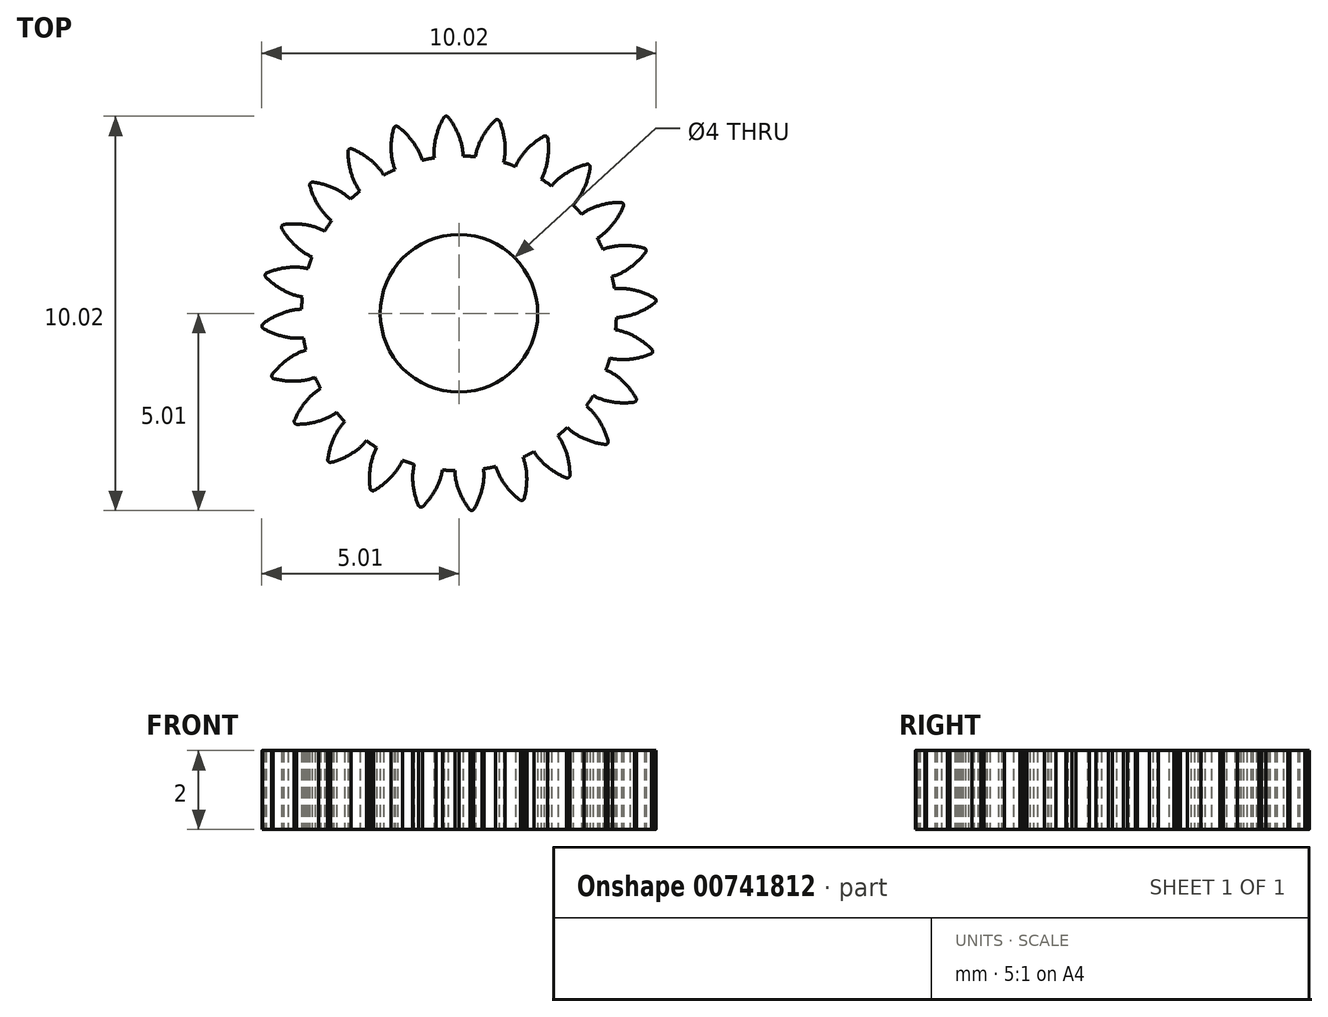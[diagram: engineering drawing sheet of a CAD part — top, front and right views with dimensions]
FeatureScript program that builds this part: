
annotation { "Feature Type Name" : "Feature", "Feature Type Description" : "" }
export const myFeature = defineFeature(function(context is Context, id is Id, definition is map)
    precondition{}
    {
        {
            var Q0;
            Q0=qCreatedBy(makeId("Top.planeOp"),FACE);
            var sketch = newSketch(context, id + "F0", { "sketchPlane" : qUnion([Q0])});
            skCircle(sketch, "E0", {"center": v(0, 0) * mm, "radius": 4 * mm});
            skCircle(sketch, "E1", {"center": v(0, 0) * mm, "radius": 4.5 * mm, "construction": true});
            skCircle(sketch, "E2", {"center": v(0, 0) * mm, "radius": 5 * mm, "construction": true});
            skLineSegment(sketch, "E3", {"start": v(0, 0) * mm, "end": v(0, 7.18) * mm, "construction": true});
            skLineSegment(sketch, "E4", {"start": v(0, 0) * mm, "end": v(-0.5, 7.73) * mm, "construction": true});
            skLineSegment(sketch, "E5", {"start": v(0, 4.5) * mm, "end": v(-8.8, 4.5) * mm, "construction": true});
            skLineSegment(sketch, "E6", {"start": v(0, 4.5) * mm, "end": v(-8.5, 1.41) * mm, "construction": true});
            skCircle(sketch, "E7", {"center": v(0, 0) * mm, "radius": 4.23 * mm, "construction": true});
            skCircle(sketch, "E8", {"center": v(0, 4.5) * mm, "radius": 1.75 * mm, "construction": true});
            skCircle(sketch, "E9", {"center": v(-1.64, 3.9) * mm, "radius": 1.75 * mm, "construction": true});
            skArc(sketch, "E10", {"start": v(0.1, 4) * mm, "mid": v(0.07, 4.25) * mm, "end": v(0, 4.5) * mm});
            skArc(sketch, "E11", {"start": v(0, 4.5) * mm, "mid": v(-0.12, 4.76) * mm, "end": v(-0.28, 5) * mm});
            skArc(sketch, "E12.MirrorCS", {"start": v(-0.59, 4.46) * mm, "mid": v(-0.5, 4.73) * mm, "end": v(-0.38, 4.99) * mm});
            skArc(sketch, "E13.MirrorCS", {"start": v(-0.63, 3.95) * mm, "mid": v(-0.63, 4.2) * mm, "end": v(-0.59, 4.46) * mm});
            skArc(sketch, "E14", {"start": v(-0.28, 5) * mm, "mid": v(-0.33, 5) * mm, "end": v(-0.38, 4.99) * mm});
            skCircle(sketch, "E15", {"center": v(0, 0) * mm, "radius": 2 * mm});
            skSolve(sketch);
        }
        {
            var Q0;
            {var subQ0=sQuery(id+"F0.wireOp",EDGE,"E0");var subQ1=makeQuery(id+"F0.imprint","INTERSECT",VERTEX,{"derivedFrom":[subQ0,sQuery(id+"F0.wireOp",EDGE,"E10")]});Q0=makeQuery(id+"F0.imprint","IMPRINT",FACE,{"disambiguationData":[TD([[makeQuery(id+"F0.imprint","IMPRINT",EDGE,{"disambiguationData":[TD([[subQ1,-1.0]])],"derivedFrom":subQ0}),1.0]])]});}
            var Q1;
            {var subQ0=sQuery(id+"F0.wireOp",EDGE,"E10");Q1=makeQuery(id+"F0.imprint","IMPRINT",FACE,{"disambiguationData":[TD([[makeQuery(id+"F0.imprint","IMPRINT",EDGE,{"derivedFrom":subQ0}),1.0]])]});}
            extrude(context, id + "F1", {"entities" : qUnion([Q0, Q1]), "depth" : 2 * mm, "offsetDistance" : 25 * mm});
        }
        {
            var Q0;
            Q0=makeQuery(id+"F1.opExtrude","SWEPT_BODY",BODY,{"disambiguationData":[OSD([sQuery(id+"F0.wireOp",EDGE,"E0"),sQuery(id+"F0.wireOp",EDGE,"E10"),sQuery(id+"F0.wireOp",EDGE,"E11"),sQuery(id+"F0.wireOp",EDGE,"E12.MirrorCS"),sQuery(id+"F0.wireOp",EDGE,"E13.MirrorCS"),sQuery(id+"F0.wireOp",EDGE,"E14")])]});
            var Q1;
            Q1=makeQuery(id+"F1.opExtrude","SWEPT_FACE",FACE,{"disambiguationData":[OSD([sQuery(id+"F0.wireOp",EDGE,"E0")])]});
            circularPattern(context, id + "F2", {"operationType" : NewBodyOperationType.ADD, "entities" : qUnion([Q0]), "axis" : qUnion([Q1]), "angle" : 360 * degree, "instanceCount" : 24, "equalSpace" : true});
        }
    });
